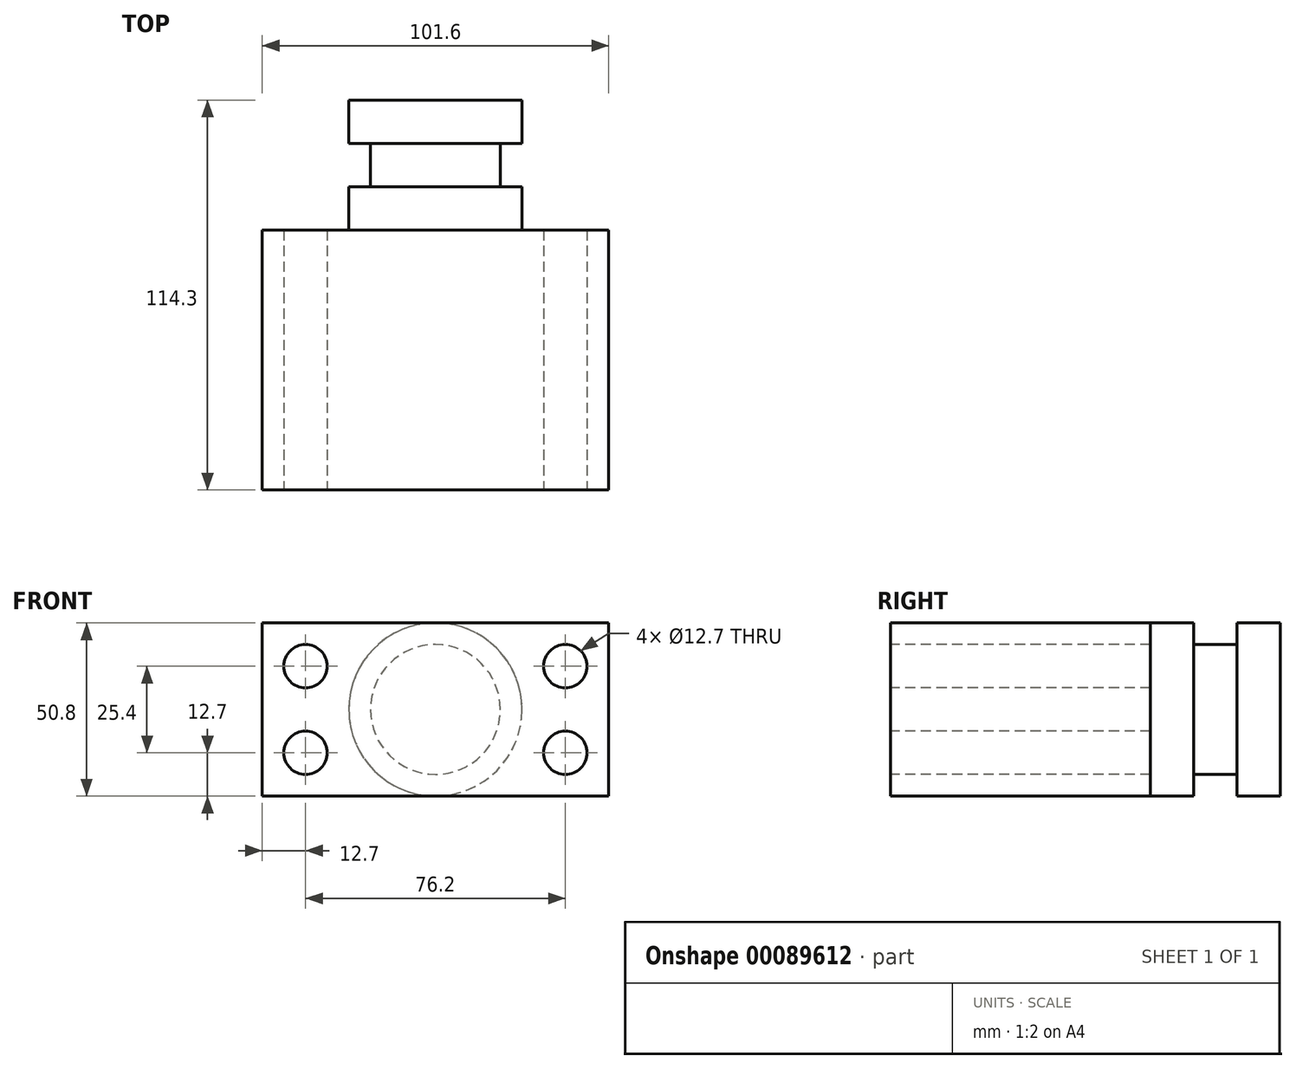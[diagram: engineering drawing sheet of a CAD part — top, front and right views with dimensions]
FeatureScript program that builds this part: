
annotation { "Feature Type Name" : "Feature", "Feature Type Description" : "" }
export const myFeature = defineFeature(function(context is Context, id is Id, definition is map)
    precondition{}
    {
        {
            var Q0;
            Q0=qCreatedBy(makeId("Front.planeOp"),FACE);
            var sketch = newSketch(context, id + "F0", { "sketchPlane" : qUnion([Q0])});
            skLineSegment(sketch, "E0", {"start": v(-50.8, 25.4) * mm, "end": v(50.8, 25.4) * mm});
            skLineSegment(sketch, "E1", {"start": v(50.8, 25.4) * mm, "end": v(50.8, -25.4) * mm});
            skLineSegment(sketch, "E2", {"start": v(50.8, -25.4) * mm, "end": v(-50.8, -25.4) * mm});
            skLineSegment(sketch, "E3", {"start": v(-50.8, -25.4) * mm, "end": v(-50.8, 25.4) * mm});
            skSolve(sketch);
        }
        {
            var Q0;
            Q0=makeQuery(id+"F0.imprint","IMPRINT",FACE,{"disambiguationData":[TD([[makeQuery(id+"F0.imprint","IMPRINT",EDGE,{"derivedFrom":sQuery(id+"F0.wireOp",EDGE,"E0")}),-1.0]])]});
            extrude(context, id + "F1", {"entities" : qUnion([Q0]), "oppositeDirection" : true, "depth" : 76.2 * mm});
        }
        {
            var Q0;
            Q0=makeQuery(id+"F1.opExtrude","CAP_FACE",FACE,{"disambiguationData":[OSD([sQuery(id+"F0.wireOp",EDGE,"E0"),sQuery(id+"F0.wireOp",EDGE,"E1"),sQuery(id+"F0.wireOp",EDGE,"E2"),sQuery(id+"F0.wireOp",EDGE,"E3")])],"isStart":true});
            var sketch = newSketch(context, id + "F2", { "sketchPlane" : qUnion([Q0])});
            skCircle(sketch, "E4", {"center": v(-38.1, 12.7) * mm, "radius": 6.35 * mm});
            skCircle(sketch, "E5", {"center": v(-38.1, -12.7) * mm, "radius": 6.35 * mm});
            skLineSegment(sketch, "E6", {"start": v(0, 42.62) * mm, "end": v(0, -39.5) * mm, "construction": true});
            skCircle(sketch, "E7.MirrorC", {"center": v(38.1, -12.7) * mm, "radius": 6.35 * mm});
            skCircle(sketch, "E8.MirrorC", {"center": v(38.1, 12.7) * mm, "radius": 6.35 * mm});
            skSolve(sketch);
        }
        {
            var Q0;
            Q0 = qSketchRegion(id + "F2", true);
            extrude(context, id + "F3", {"entities" : qUnion([Q0]), "operationType" : NewBodyOperationType.REMOVE, "endBound" : BoundingType.THROUGH_ALL, "oppositeDirection" : true, "depth" : 25.4 * mm});
        }
        {
            var Q0;
            Q0=qCreatedBy(makeId("Top.planeOp"),FACE);
            var sketch = newSketch(context, id + "F4", { "sketchPlane" : qUnion([Q0])});
            skLineSegment(sketch, "E9", {"start": v(0, 76.2) * mm, "end": v(0, 114.3) * mm});
            skLineSegment(sketch, "E10", {"start": v(0, 114.3) * mm, "end": v(25.4, 114.3) * mm});
            skLineSegment(sketch, "E11", {"start": v(25.4, 114.3) * mm, "end": v(25.4, 76.2) * mm});
            skLineSegment(sketch, "E12", {"start": v(25.4, 76.2) * mm, "end": v(0, 76.2) * mm});
            skSolve(sketch);
        }
        {
            var Q0;
            Q0=makeQuery(id+"F4.imprint","IMPRINT",FACE,{"disambiguationData":[TD([[makeQuery(id+"F4.imprint","IMPRINT",EDGE,{"derivedFrom":sQuery(id+"F4.wireOp",EDGE,"E9")}),-1.0]])]});
            var Q1;
            Q1=sQuery(id+"F4.wireOp",EDGE,"E9");
            revolve(context, id + "F5", {"operationType" : NewBodyOperationType.ADD, "entities" : qUnion([Q0]), "axis" : qUnion([Q1]), "revolveType" : RevolveType.FULL});
        }
        {
            var Q0;
            Q0=qCreatedBy(makeId("Top.planeOp"),FACE);
            var sketch = newSketch(context, id + "F6", { "sketchPlane" : qUnion([Q0])});
            skLineSegment(sketch, "E13", {"start": v(0, 0) * mm, "end": v(0, 140.43) * mm, "construction": true});
            skLineSegment(sketch, "E14", {"start": v(25.4, 101.6) * mm, "end": v(25.4, 88.9) * mm});
            skLineSegment(sketch, "E15", {"start": v(25.4, 101.6) * mm, "end": v(19.05, 101.6) * mm});
            skLineSegment(sketch, "E16", {"start": v(19.05, 101.6) * mm, "end": v(19.05, 88.9) * mm});
            skLineSegment(sketch, "E17", {"start": v(19.05, 88.9) * mm, "end": v(25.4, 88.9) * mm});
            skSolve(sketch);
        }
        {
            var Q0;
            Q0 = qSketchRegion(id + "F6", true);
            var Q1;
            Q1=sQuery(id+"F6.wireOp",EDGE,"E13");
            revolve(context, id + "F7", {"operationType" : NewBodyOperationType.REMOVE, "entities" : qUnion([Q0]), "axis" : qUnion([Q1]), "revolveType" : RevolveType.FULL, "oppositeDirection" : true});
        }
    });
